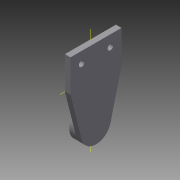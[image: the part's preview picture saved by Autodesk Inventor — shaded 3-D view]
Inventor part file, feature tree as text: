
AUTODESK INVENTOR PART (.ipt)
format: ipt  version: 2015 (Build 190159000, 159)  size: 97,792 bytes
history: native  units: mm
features: extrude x2, hole x2, sketch x2
ambient origin geometry x8: Origin, YZ Plane, XZ Plane, XY Plane, X Axis, Y Axis, Z Axis, Center Point
bodies: Solid1 (feature_tree)
feature tree (6):
  extrude  "Extrusion1"  Depth=55.0mm
  extrude  "Extrusion2"  Depth=16.0mm
  hole  "Hole1"  [1 undecoded]
  hole  "Hole2"  [1 undecoded]
  sketch  "Sketch1"  dims[d0=55.0mm d1=35.0mm]
  sketch  "Sketch2"  dims[d2=18.0mm d3=16.0mm d4=60.0mm d5=6.0mm d6=0.0mm d7=7.0mm d8=0.0mm d9=12.0mm d10=12.0mm d11=6.0mm d12=6.0mm d13=4.0mm d14=2.0mm d15=90.0deg d16=8.0mm d17=20.594885mm d18=12.0mm d19=12.0mm d20=6.0mm d21=6.0mm d22=4.0mm d23=2.0mm d24=90.0deg d25=8.0mm d26=20.594885mm]
note: 2 required parameter values undecoded (feature->parameter linkage not recoverable at this tier; creation-order binding heuristic only, values carry confidence <= 0.55)
